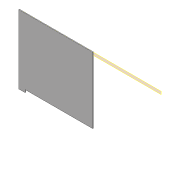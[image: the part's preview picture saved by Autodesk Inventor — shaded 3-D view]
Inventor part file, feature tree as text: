
AUTODESK INVENTOR PART (.ipt)
format: ipt  version: 2020 (Build 240168000, 168)  size: 77,824 bytes
history: native  units: mm
features: other x8, extrude x1, sketch x1
ambient origin geometry x8: Origin, YZ Plane, XZ Plane, XY Plane, X Axis, Y Axis, Z Axis, Center Point
bodies: Body1 (feature_tree)
feature tree (10):
  other  "Sólido1"
  other  "Plano de trabalho1"
  extrude  "Extrusão1"  [1 undecoded]
  sketch  "Esboço1"  dims[d0=1.0mm d1=0.0mm]
  other  "Referência1"
  other  "<userpath>\OneDrive\Área de Trabalho\Calorimetro 2022\Inventor\Calorímetro.iam"
  other  "Calorímetro.iam"
  other  "Base:1"
  other  "parte_superior:1"
  other  "Base:2"
note: 1 required parameter value undecoded (feature->parameter linkage not recoverable at this tier; creation-order binding heuristic only, values carry confidence <= 0.55)
